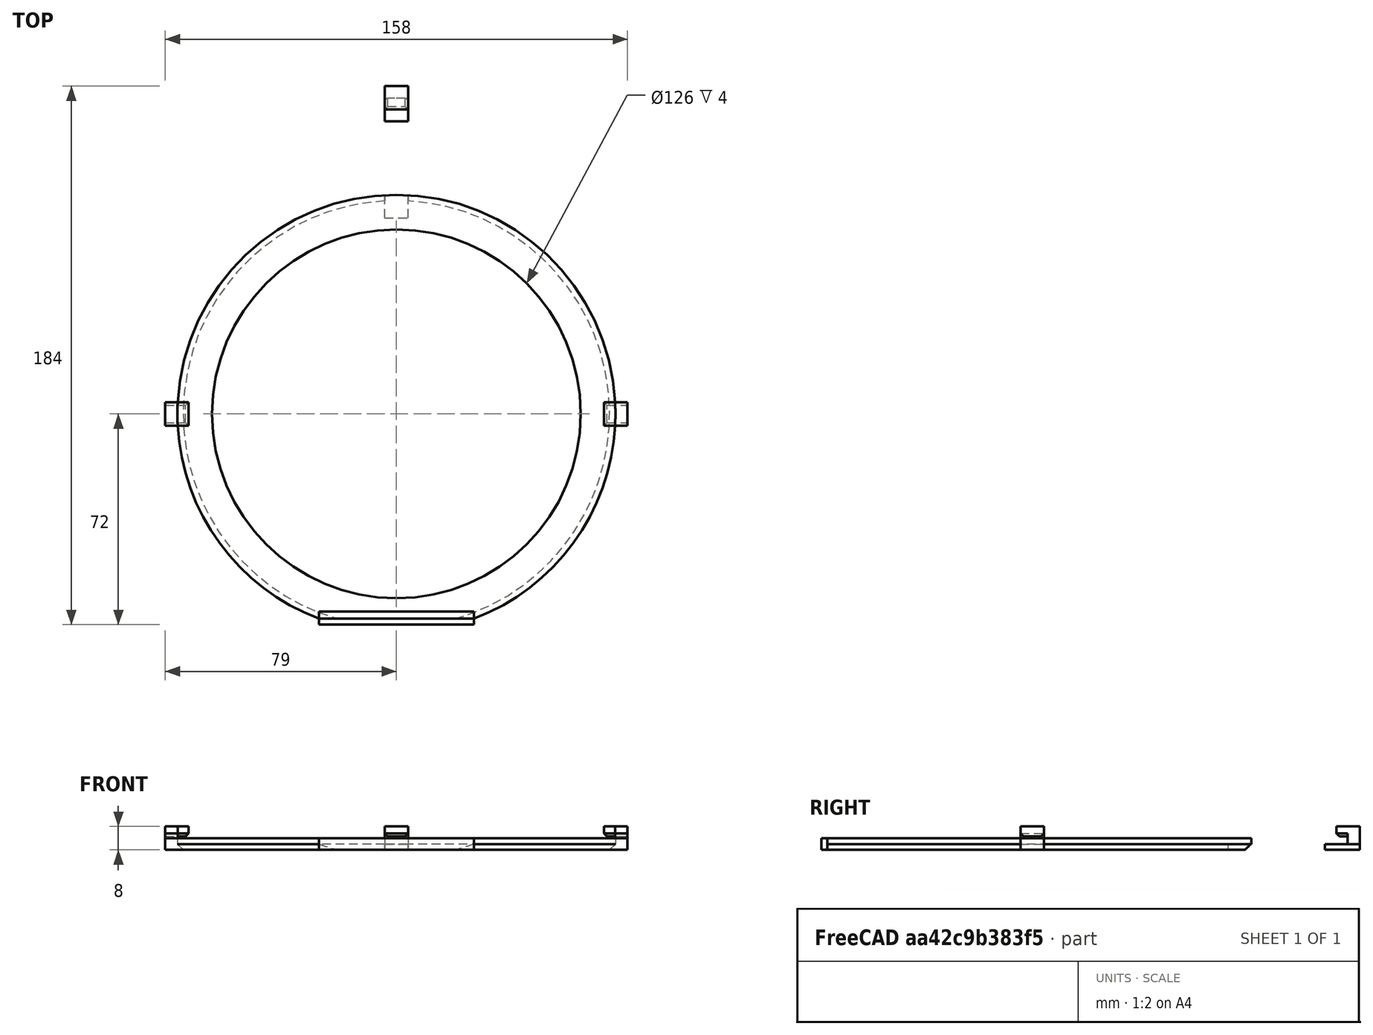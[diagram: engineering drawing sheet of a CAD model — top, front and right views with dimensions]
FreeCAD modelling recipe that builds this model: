
FCSTD DOCUMENT  (FreeCAD 0.19R0.19.2)
Label: waferHolder_008
License: All rights reserved
LicenseURL: http://en.wikipedia.org/wiki/All_rights_reserved
objects: Part::Box×17, Part::Chamfer×13, Part::Cut×8, Sketcher::SketchObject×5, Part::Extrusion×5, Part::MultiFuse×2
note: 50 computed .brp shape members not serialized (recipe doc carries the construction recipe); baked Part::Feature solids carry a one-line shape summary decoded from their .brp

FEATURE [Sketcher::SketchObject] Sketch
  FullyConstrained = true
  sketch-geometry (3):
    g0: Circle CenterX=-3.1415e-12 CenterY=5.6243e-12 CenterZ=0 NormalX=0 NormalY=0 NormalZ=1 AngleXU=0 Radius=63
    g1: ArcOfCircle CenterX=-3.1415e-12 CenterY=5.6243e-12 CenterZ=0 NormalX=0 NormalY=0 NormalZ=1 AngleXU=0 Radius=74.8482 StartAngle=5.07429 EndAngle=10.6337
    g2: LineSegment StartX=-26.5 StartY=-70.0001 StartZ=0 EndX=26.5 EndY=-70.0001 EndZ=0
  constraints (6):
    c: Block(g0)
    c: Coincident(g1,g0)
    c: Block(g1)
    c: Coincident(g2,g1)
    c: Coincident(g2,g1)
    c: Horizontal(g2)
FEATURE [Part::Box] Box  label="holderBitLeft"
  AttacherType = Attacher::AttachEngine3D
  Height = 4
  Length = 8
  Placement = pos=(-79,-4,0) rot=(0,0,1;0rad)
  Width = 8
FEATURE [Part::Box] Box001  label="bitHolderTopCutout"
  AttacherType = Attacher::AttachEngine3D
  Height = 4
  Length = 8
  Placement = pos=(-4,67,-2) rot=(0,0,1;0rad)
  Width = 12
FEATURE [Part::Extrusion] Extrude  label="mainHolderRing"
  Base = -> Sketch
  Dir = (0,0,1)
  DirMode = 2
  FaceMakerClass = Part::FaceMakerBullseye
  LengthFwd = 4
  LengthRev = 0
  Solid = true
  Symmetric = false
FEATURE [Part::Box] Box002  label="holderBitRight"
  AttacherType = Attacher::AttachEngine3D
  Height = 4
  Length = 8
  Placement = pos=(71,-4,0) rot=(0,0,1;0rad)
  Width = 8
FEATURE [Part::Box] Box003  label="bitHolderTop"
  AttacherType = Attacher::AttachEngine3D
  Height = 2
  Length = 8
  Placement = pos=(-4,100,0) rot=(0,0,1;0rad)
  Width = 12
FEATURE [Part::Chamfer] Chamfer
  Base = -> Extrude
  Edges = 1 edges r=2: [Edge3]
FEATURE [Part::Cut] Cut  label="mainHolderRing001"
  Base = -> Chamfer
  Tool = -> Box001
FEATURE [Part::Box] Box004  label="holderBitLeft001"
  AttacherType = Attacher::AttachEngine3D
  Height = 4
  Length = 6
  Placement = pos=(-79,-4,0) rot=(0,0,1;0rad)
  Width = 8
FEATURE [Part::Box] Box005  label="holderBitright002"
  AttacherType = Attacher::AttachEngine3D
  Height = 4
  Length = 6
  Placement = pos=(73,-4,0) rot=(0,0,1;0rad)
  Width = 8
FEATURE [Part::MultiFuse] Fusion  label="holders"
  Shapes = -> [Box004,Box005]
FEATURE [Sketcher::SketchObject] Sketch001
  FullyConstrained = true
  sketch-geometry (3):
    g0: Circle CenterX=-3.1415e-12 CenterY=5.6243e-12 CenterZ=0 NormalX=0 NormalY=0 NormalZ=1 AngleXU=0 Radius=63
    g1: ArcOfCircle CenterX=-3.1415e-12 CenterY=5.6243e-12 CenterZ=0 NormalX=0 NormalY=0 NormalZ=1 AngleXU=0 Radius=74.8482 StartAngle=5.07429 EndAngle=10.6337
    g2: LineSegment StartX=-26.5 StartY=-70.0001 StartZ=0 EndX=26.5 EndY=-70.0001 EndZ=0
  constraints (6):
    c: Block(g0)
    c: Coincident(g1,g0)
    c: Block(g1)
    c: Coincident(g2,g1)
    c: Coincident(g2,g1)
    c: Horizontal(g2)
FEATURE [Part::Extrusion] Extrude001  label="mainHolderRing002"
  Base = -> Sketch001
  Dir = (0,0,1)
  DirMode = 2
  FaceMakerClass = Part::FaceMakerBullseye
  LengthFwd = 4
  LengthRev = 0
  Solid = true
  Symmetric = false
FEATURE [Part::Cut] Cut001  label="leftAndRightHolderBits"
  Base = -> Fusion
  Placement = pos=(0,0,4) rot=(0,0,1;0rad)
  Tool = -> Extrude001
FEATURE [Part::Box] Box006  label="holderBitLeft002"
  AttacherType = Attacher::AttachEngine3D
  Height = 3.4
  Length = 8
  Placement = pos=(-79,-4,4.6) rot=(0,0,1;0rad)
  Width = 8
FEATURE [Part::Box] Box007  label="holderBitRight002"
  AttacherType = Attacher::AttachEngine3D
  Height = 3.4
  Length = 8
  Placement = pos=(71,-4,4.6) rot=(0,0,1;0rad)
  Width = 8
FEATURE [Part::Box] Box008  label="holderBitLeft003"
  AttacherType = Attacher::AttachEngine3D
  Height = 2
  Length = 8
  Placement = pos=(-4,71,2) rot=(0,0,1;0rad)
  Width = 8
FEATURE [Part::Box] Box009  label="bitHolderTopCutout001"
  AttacherType = Attacher::AttachEngine3D
  Height = 4
  Length = 8
  Placement = pos=(-4,67,-2) rot=(0,0,1;0rad)
  Width = 12
FEATURE [Sketcher::SketchObject] Sketch002
  FullyConstrained = true
  sketch-geometry (3):
    g0: Circle CenterX=-3.1415e-12 CenterY=5.6243e-12 CenterZ=0 NormalX=0 NormalY=0 NormalZ=1 AngleXU=0 Radius=63
    g1: ArcOfCircle CenterX=-3.1415e-12 CenterY=5.6243e-12 CenterZ=0 NormalX=0 NormalY=0 NormalZ=1 AngleXU=0 Radius=74.8482 StartAngle=5.07429 EndAngle=10.6337
    g2: LineSegment StartX=-26.5 StartY=-70.0001 StartZ=0 EndX=26.5 EndY=-70.0001 EndZ=0
  constraints (6):
    c: Block(g0)
    c: Coincident(g1,g0)
    c: Block(g1)
    c: Coincident(g2,g1)
    c: Coincident(g2,g1)
    c: Horizontal(g2)
FEATURE [Part::Extrusion] Extrude002  label="mainHolderRing003"
  Base = -> Sketch002
  Dir = (0,0,1)
  DirMode = 2
  FaceMakerClass = Part::FaceMakerBullseye
  LengthFwd = 4
  LengthRev = 0
  Solid = true
  Symmetric = false
FEATURE [Part::Chamfer] Chamfer001
  Base = -> Extrude002
  Edges = 1 edges r=2: [Edge3]
FEATURE [Part::Cut] Cut002  label="mainHolderRing004"
  Base = -> Chamfer001
  Tool = -> Box009
FEATURE [Part::Cut] Cut003  label="bitHolderTop001"
  Base = -> Box008
  Tool = -> Cut002
FEATURE [Part::Box] Box010  label="holderBitLeft004"
  AttacherType = Attacher::AttachEngine3D
  Height = 2
  Length = 8
  Placement = pos=(-4,71,2) rot=(0,0,1;0rad)
  Width = 8
FEATURE [Part::Box] Box011  label="bitHolderTopCutout002"
  AttacherType = Attacher::AttachEngine3D
  Height = 4
  Length = 8
  Placement = pos=(-4,67,-2) rot=(0,0,1;0rad)
  Width = 12
FEATURE [Sketcher::SketchObject] Sketch003
  FullyConstrained = true
  sketch-geometry (3):
    g0: Circle CenterX=-3.1415e-12 CenterY=5.6243e-12 CenterZ=0 NormalX=0 NormalY=0 NormalZ=1 AngleXU=0 Radius=63
    g1: ArcOfCircle CenterX=-3.1415e-12 CenterY=5.6243e-12 CenterZ=0 NormalX=0 NormalY=0 NormalZ=1 AngleXU=0 Radius=74.8482 StartAngle=5.07429 EndAngle=10.6337
    g2: LineSegment StartX=-26.5 StartY=-70.0001 StartZ=0 EndX=26.5 EndY=-70.0001 EndZ=0
  constraints (6):
    c: Block(g0)
    c: Coincident(g1,g0)
    c: Block(g1)
    c: Coincident(g2,g1)
    c: Coincident(g2,g1)
    c: Horizontal(g2)
FEATURE [Part::Extrusion] Extrude003  label="mainHolderRing006"
  Base = -> Sketch003
  Dir = (0,0,1)
  DirMode = 2
  FaceMakerClass = Part::FaceMakerBullseye
  LengthFwd = 4
  LengthRev = 0
  Solid = true
  Symmetric = false
FEATURE [Part::Chamfer] Chamfer002
  Base = -> Extrude003
  Edges = 1 edges r=2: [Edge3]
FEATURE [Part::Cut] Cut005  label="mainHolderRing005"
  Base = -> Chamfer002
  Tool = -> Box011
FEATURE [Part::Cut] Cut004  label="bitHolderTop002"
  Base = -> Box010
  Placement = pos=(0,0,2) rot=(0,0,1;0rad)
  Tool = -> Cut005
FEATURE [Part::Box] Box012  label="holderBitLeft005"
  AttacherType = Attacher::AttachEngine3D
  Height = 2
  Length = 8
  Placement = pos=(-4,71,2) rot=(0,0,1;0rad)
  Width = 8
FEATURE [Part::Box] Box013  label="bitHolderTopCutout003"
  AttacherType = Attacher::AttachEngine3D
  Height = 4
  Length = 8
  Placement = pos=(-4,67,-2) rot=(0,0,1;0rad)
  Width = 12
FEATURE [Sketcher::SketchObject] Sketch004
  FullyConstrained = true
  sketch-geometry (3):
    g0: Circle CenterX=-3.1415e-12 CenterY=5.6243e-12 CenterZ=0 NormalX=0 NormalY=0 NormalZ=1 AngleXU=0 Radius=63
    g1: ArcOfCircle CenterX=-3.1415e-12 CenterY=5.6243e-12 CenterZ=0 NormalX=0 NormalY=0 NormalZ=1 AngleXU=0 Radius=74.8482 StartAngle=5.07429 EndAngle=10.6337
    g2: LineSegment StartX=-26.5 StartY=-70.0001 StartZ=0 EndX=26.5 EndY=-70.0001 EndZ=0
  constraints (6):
    c: Block(g0)
    c: Coincident(g1,g0)
    c: Block(g1)
    c: Coincident(g2,g1)
    c: Coincident(g2,g1)
    c: Horizontal(g2)
FEATURE [Part::Extrusion] Extrude004  label="mainHolderRing008"
  Base = -> Sketch004
  Dir = (0,0,1)
  DirMode = 2
  FaceMakerClass = Part::FaceMakerBullseye
  LengthFwd = 4
  LengthRev = 0
  Solid = true
  Symmetric = false
FEATURE [Part::Chamfer] Chamfer003
  Base = -> Extrude004
  Edges = 1 edges r=2: [Edge3]
FEATURE [Part::Cut] Cut007  label="mainHolderRing007"
  Base = -> Chamfer003
  Tool = -> Box013
FEATURE [Part::Cut] Cut006  label="bitHolderTop003"
  Base = -> Box012
  Placement = pos=(0,0,4) rot=(0,0,1;0rad)
  Tool = -> Cut007
FEATURE [Part::Box] Box014  label="bitHoldertop006"
  AttacherType = Attacher::AttachEngine3D
  Height = 3.4
  Length = 8
  Placement = pos=(-4,71,4.6) rot=(0,0,1;0rad)
  Width = 8
FEATURE [Part::MultiFuse] Fusion001  label="holderTop"
  Placement = pos=(0,33,0) rot=(0,0,1;0rad)
  Shapes = -> [Cut003,Cut004,Cut006,Box014]
FEATURE [Part::Chamfer] Chamfer004
  Base = -> Fusion001
  Edges = 1 edges r=1: [Edge16]
FEATURE [Part::Chamfer] Chamfer005
  Base = -> Box006
  Edges = 1 edges r=1: [Edge8]
FEATURE [Part::Chamfer] Chamfer006
  Base = -> Box007
  Edges = 1 edges r=1: [Edge4]
FEATURE [Part::Chamfer] Chamfer007
  Base = -> Chamfer006
  Edges = 1 edges r=1: [Edge13]
FEATURE [Part::Chamfer] Chamfer008
  Base = -> Chamfer007
  Edges = 1 edges r=1: [Edge5]
FEATURE [Part::Chamfer] Chamfer009
  Base = -> Chamfer004
  Edges = 1 edges r=1: [Edge1]
FEATURE [Part::Chamfer] Chamfer010
  Base = -> Chamfer009
  Edges = 1 edges r=1: [Edge32]
FEATURE [Part::Chamfer] Chamfer011
  Base = -> Chamfer005
  Edges = 1 edges r=1: [Edge5]
FEATURE [Part::Chamfer] Chamfer012
  Base = -> Chamfer011
  Edges = 1 edges r=1: [Edge16]
FEATURE [Part::Box] Box015  label="holderBitLeft006"
  AttacherType = Attacher::AttachEngine3D
  Height = 4
  Length = 53
  Placement = pos=(-26.5,-72,0) rot=(0,0,1;0rad)
  Width = 4.5
FEATURE [Part::Box] Box016  label="holderBitLeft007"
  AttacherType = Attacher::AttachEngine3D
  Height = 4
  Length = 53
  Placement = pos=(-26.5,-72,0) rot=(0,0,1;0rad)
  Width = 2
